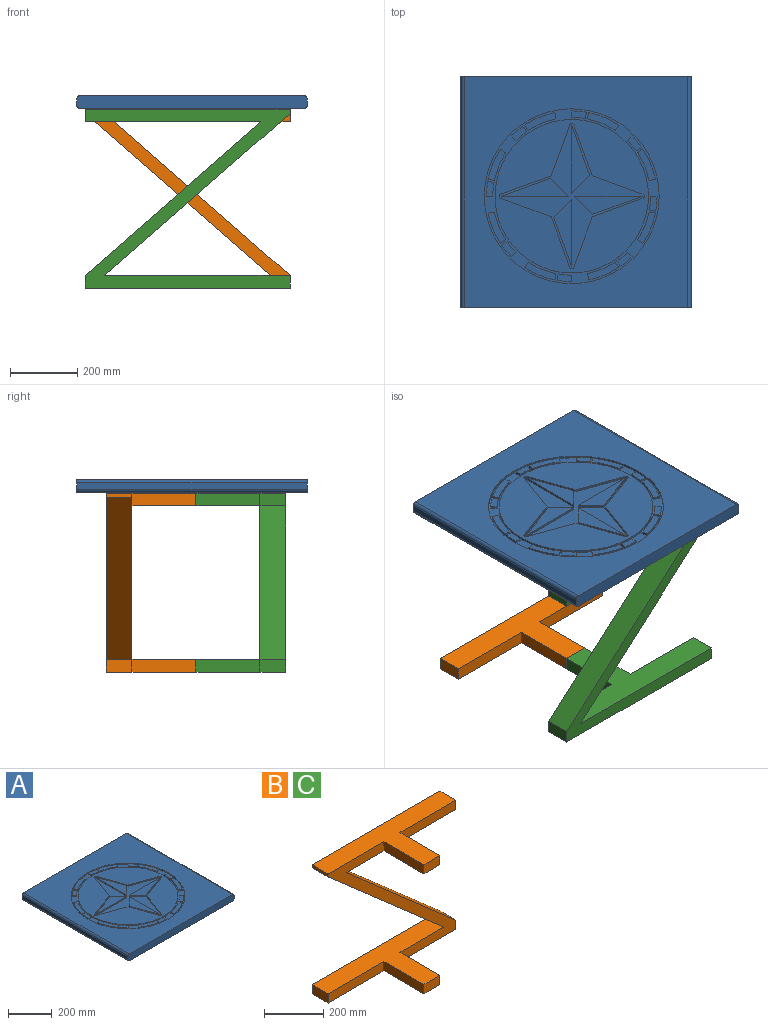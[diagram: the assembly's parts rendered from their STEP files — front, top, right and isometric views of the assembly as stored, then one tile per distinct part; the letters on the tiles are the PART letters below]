
ASSEMBLY  parts=3 mates=1
PART A: 123 faces, bbox 685.8x685.8x38.1 mm
  f0: plane 457.2x457.2mm, normal (0,0,1), area 108640mm2, adj f76,f96,f97,f98,f99,f100,f101,f102
  f1: plane 685.8x666.75mm, normal (0,0,1), area 244313.3mm2, adj f3,f5,f9,f10,f59
  f2: plane 685.8x19.05mm, normal (-1,0,0), area 13064.5mm2, adj f3,f5,f8,f10
  f3: plane 685.8x38.1mm, normal (0,-1,0), area 26051.1mm2, adj f1,f2,f4,f6,f7,f8,f9,f10
  f4: plane 685.8x19.05mm, normal (1,0,0), area 13064.5mm2, adj f3,f5,f7,f9
  f5: plane 685.8x38.1mm, normal (0,1,0), area 26051.1mm2, adj f1,f2,f4,f6,f7,f8,f9,f10
  f6: plane 685.8x666.75mm, normal (0,0,-1), area 457257.1mm2, adj f3,f5,f7,f8
  f7: cylinder r=9.53mm len=685.8mm, axis (0,1,0), area 10260.8mm2, adj f3,f4,f5,f6
  f8: cylinder r=9.53mm len=685.8mm, axis (0,-1,0), area 10260.8mm2, adj f2,f3,f5,f6
  f9: cylinder r=9.53mm len=685.8mm, axis (0,-1,0), area 10260.8mm2, adj f1,f3,f4,f5
  f10: cylinder r=9.53mm len=685.8mm, axis (0,1,0), area 10260.8mm2, adj f1,f2,f3,f5
  f11: cylinder r=254mm len=90.1mm, axis (0,0,1), area 623.1mm2, adj f12,f60,f77,f93
  f12: plane 18.77x6.35mm, normal (0.17,-0.98,0), area 121mm2, adj f11,f13,f77,f93
  f13: cylinder r=234.95mm len=82.47mm, axis (0,0,1), area 570.3mm2, adj f12,f60,f77,f93
  f14: cylinder r=254mm len=33.92mm, axis (0,0,1), area 281.5mm2, adj f15,f61,f77,f92
  f15: plane 15.61x10.93mm, normal (0.57,-0.82,0), area 121mm2, adj f14,f16,f77,f92
  f16: cylinder r=234.95mm len=31.37mm, axis (0,0,1), area 260.4mm2, adj f15,f61,f77,f92
  f17: cylinder r=254mm len=33.92mm, axis (0,0,1), area 281.5mm2, adj f18,f62,f77,f91
  f18: plane 15.61x10.93mm, normal (0.82,0.57,0), area 121mm2, adj f17,f19,f77,f91
  f19: cylinder r=234.95mm len=31.37mm, axis (0,0,1), area 260.4mm2, adj f18,f62,f77,f91
  f20: cylinder r=254mm len=90.1mm, axis (0,0,1), area 623.1mm2, adj f21,f63,f77,f90
  f21: plane 15.61x10.93mm, normal (0.57,0.82,0), area 121mm2, adj f20,f22,f77,f90
  f22: cylinder r=234.95mm len=82.47mm, axis (0,0,1), area 570.3mm2, adj f21,f63,f77,f90
  f23: cylinder r=254mm len=44.11mm, axis (0,0,1), area 281.5mm2, adj f24,f64,f77,f89
  f24: plane 18.76x6.35mm, normal (0.17,0.98,0), area 121mm2, adj f23,f25,f77,f89
  f25: cylinder r=234.95mm len=40.8mm, axis (0,0,1), area 260.4mm2, adj f24,f64,f77,f89
  f26: cylinder r=254mm len=90.1mm, axis (0,0,1), area 623.1mm2, adj f27,f65,f77,f88
  f27: plane 18.77x6.35mm, normal (-0.17,0.98,0), area 121mm2, adj f26,f28,f77,f88
  f28: cylinder r=234.95mm len=82.47mm, axis (0,0,1), area 570.3mm2, adj f27,f65,f77,f88
  f29: cylinder r=254mm len=33.92mm, axis (0,0,1), area 281.5mm2, adj f30,f66,f77,f87
  f30: plane 15.61x10.93mm, normal (-0.57,0.82,0), area 121mm2, adj f29,f31,f77,f87
  f31: cylinder r=234.95mm len=31.37mm, axis (0,0,1), area 260.4mm2, adj f30,f66,f77,f87
  f32: cylinder r=254mm len=90.1mm, axis (0,0,1), area 623.1mm2, adj f33,f67,f77,f86
  f33: plane 15.61x10.93mm, normal (-0.82,0.57,0), area 121mm2, adj f32,f34,f77,f86
  f34: cylinder r=234.95mm len=82.47mm, axis (0,0,1), area 570.3mm2, adj f33,f67,f77,f86
  f35: cylinder r=254mm len=44.11mm, axis (0,0,1), area 281.5mm2, adj f36,f68,f77,f85
  f36: plane 18.76x6.35mm, normal (-0.98,0.17,0), area 121mm2, adj f35,f37,f77,f85
  f37: cylinder r=234.95mm len=40.8mm, axis (0,0,1), area 260.4mm2, adj f36,f68,f77,f85
  f38: cylinder r=254mm len=90.1mm, axis (0,0,1), area 623.1mm2, adj f39,f69,f77,f84
  f39: plane 18.77x6.35mm, normal (-0.98,-0.17,0), area 121mm2, adj f38,f40,f77,f84
  f40: cylinder r=234.95mm len=82.47mm, axis (0,0,1), area 570.3mm2, adj f39,f69,f77,f84
  f41: cylinder r=254mm len=33.92mm, axis (0,0,1), area 281.5mm2, adj f42,f70,f77,f83
  f42: plane 15.61x10.93mm, normal (-0.82,-0.57,0), area 121mm2, adj f41,f43,f77,f83
  f43: cylinder r=234.95mm len=31.37mm, axis (0,0,1), area 260.4mm2, adj f42,f70,f77,f83
  f44: cylinder r=254mm len=90.1mm, axis (0,0,1), area 623.1mm2, adj f45,f71,f77,f82
  f45: plane 15.61x10.93mm, normal (-0.57,-0.82,0), area 121mm2, adj f44,f46,f77,f82
  f46: cylinder r=234.95mm len=82.47mm, axis (0,0,1), area 570.3mm2, adj f45,f71,f77,f82
  f47: cylinder r=254mm len=44.11mm, axis (0,0,1), area 281.5mm2, adj f48,f72,f77,f81
  f48: plane 18.76x6.35mm, normal (-0.17,-0.98,0), area 121mm2, adj f47,f49,f77,f81
  f49: cylinder r=234.95mm len=40.8mm, axis (0,0,1), area 260.4mm2, adj f48,f72,f77,f81
  f50: cylinder r=234.95mm len=82.47mm, axis (0,0,1), area 570.3mm2, adj f51,f73,f77,f80
  f51: plane 18.77x6.35mm, normal (-0.98,0.17,0), area 121mm2, adj f50,f52,f77,f80
  f52: cylinder r=254mm len=90.1mm, axis (0,0,1), area 623.1mm2, adj f51,f73,f77,f80
  f53: plane 18.77x6.35mm, normal (0.98,0.17,0), area 121mm2, adj f54,f74,f77,f79
  f54: cylinder r=234.95mm len=82.47mm, axis (0,0,1), area 570.3mm2, adj f53,f55,f77,f79
  f55: plane 15.61x10.93mm, normal (-0.82,-0.57,0), area 121mm2, adj f54,f74,f77,f79
  f56: cylinder r=234.95mm len=40.8mm, axis (0,0,1), area 260.4mm2, adj f57,f75,f77,f78
  f57: plane 19.05x6.35mm, normal (-1,0,0), area 121mm2, adj f56,f58,f77,f78
  f58: cylinder r=254mm len=44.11mm, axis (0,0,1), area 281.5mm2, adj f57,f75,f77,f78
  f59: cylinder r=260.35mm len=520.7mm, axis (0,0,1), area 10387.5mm2, adj f1,f77
  f60: plane 15.61x10.93mm, normal (-0.57,0.82,0), area 121mm2, adj f11,f13,f77,f93
  f61: plane 13.47x13.47mm, normal (-0.71,0.71,0), area 121mm2, adj f14,f16,f77,f92
  f62: plane 13.47x13.47mm, normal (-0.71,-0.71,0), area 121mm2, adj f17,f19,f77,f91
  f63: plane 18.77x6.35mm, normal (-0.17,-0.98,0), area 121mm2, adj f20,f22,f77,f90
  f64: plane 19.05x6.35mm, normal (0,-1,0), area 121mm2, adj f23,f25,f77,f89
  f65: plane 15.61x10.93mm, normal (0.57,-0.82,0), area 121mm2, adj f26,f28,f77,f88
  f66: plane 13.47x13.47mm, normal (0.71,-0.71,0), area 121mm2, adj f29,f31,f77,f87
  f67: plane 18.77x6.35mm, normal (0.98,-0.17,0), area 121mm2, adj f32,f34,f77,f86
  f68: plane 19.05x6.35mm, normal (1,0,0), area 121mm2, adj f35,f37,f77,f85
  f69: plane 15.61x10.93mm, normal (0.82,0.57,0), area 121mm2, adj f38,f40,f77,f84
  f70: plane 13.47x13.47mm, normal (0.71,0.71,0), area 121mm2, adj f41,f43,f77,f83
  f71: plane 18.77x6.35mm, normal (0.17,0.98,0), area 121mm2, adj f44,f46,f77,f82
  f72: plane 19.05x6.35mm, normal (0,1,0), area 121mm2, adj f47,f49,f77,f81
  f73: plane 15.61x10.93mm, normal (0.82,-0.57,0), area 121mm2, adj f50,f52,f77,f80
  f74: cylinder r=254mm len=90.1mm, axis (0,0,1), area 623.1mm2, adj f53,f55,f77,f79
  f75: plane 18.76x6.35mm, normal (0.98,-0.17,0), area 121mm2, adj f56,f58,f77,f78
  f76: cylinder r=228.6mm len=457.2mm, axis (0,0,1), area 9120.7mm2, adj f0,f77
  f77: plane 520.7x520.7mm, normal (0,0,1), area 27946.7mm2, adj f11,f12,f13,f14,f15,f16,f17,f18
  f78: plane 44.11x22.62mm, normal (0,0,1), area 812.8mm2, adj f56,f57,f58,f75
  f79: plane 93.4x52.93mm, normal (0,0,1), area 1790.1mm2, adj f53,f54,f55,f74
  f80: plane 93.4x52.93mm, normal (0,0,1), area 1790.1mm2, adj f50,f51,f52,f73
  f81: plane 44.11x22.62mm, normal (0,0,1), area 812.8mm2, adj f47,f48,f49,f72
  f82: plane 93.4x52.93mm, normal (0,0,1), area 1790.1mm2, adj f44,f45,f46,f71
  f83: plane 44.84x41.93mm, normal (0,0,1), area 812.8mm2, adj f41,f42,f43,f70
  f84: plane 93.4x52.93mm, normal (0,0,1), area 1790.1mm2, adj f38,f39,f40,f69
  f85: plane 44.11x22.62mm, normal (0,0,1), area 812.8mm2, adj f35,f36,f37,f68
  f86: plane 93.4x52.93mm, normal (0,0,1), area 1790.1mm2, adj f32,f33,f34,f67
  f87: plane 44.84x41.93mm, normal (0,0,1), area 812.8mm2, adj f29,f30,f31,f66
  f88: plane 93.4x52.93mm, normal (0,0,1), area 1790.1mm2, adj f26,f27,f28,f65
  f89: plane 44.11x22.62mm, normal (0,0,1), area 812.8mm2, adj f23,f24,f25,f64
  f90: plane 93.4x52.93mm, normal (0,0,1), area 1790.1mm2, adj f20,f21,f22,f63
  f91: plane 44.84x41.93mm, normal (0,0,1), area 812.8mm2, adj f17,f18,f19,f62
  f92: plane 44.84x41.93mm, normal (0,0,1), area 812.8mm2, adj f14,f15,f16,f61
  f93: plane 93.4x52.93mm, normal (0,0,1), area 1790.1mm2, adj f11,f12,f13,f60
  f94: plane 147.4x53.65mm, normal (-0.34,0.94,0), area 996.1mm2, adj f95,f114,f115,f116
  f95: plane 53.65x53.65mm, normal (0.71,0.71,0), area 481.8mm2, adj f94,f114,f115,f116
  f96: plane 151.2x55.03mm, normal (-0.34,0.94,0), area 1021.8mm2, adj f0,f97,f112,f116
  f97: cylinder r=6.35mm len=11.93mm, axis (0,0,1), area 98.5mm2, adj f0,f96,f98,f116
  f98: plane 151.2x55.03mm, normal (-0.34,-0.94,0), area 1021.8mm2, adj f0,f97,f99,f116
  f99: plane 151.2x55.03mm, normal (-0.94,-0.34,0), area 1021.8mm2, adj f0,f98,f100,f116
  f100: cylinder r=6.35mm len=11.93mm, axis (0,0,1), area 98.5mm2, adj f0,f99,f101,f116
  f101: plane 151.2x55.03mm, normal (0.94,-0.34,0), area 1021.8mm2, adj f0,f100,f102,f116
  f102: plane 151.2x55.03mm, normal (0.34,-0.94,0), area 1021.8mm2, adj f0,f101,f103,f116
  f103: cylinder r=6.35mm len=11.93mm, axis (0,0,1), area 98.5mm2, adj f0,f102,f104,f116
  f104: plane 151.2x55.03mm, normal (0.34,0.94,0), area 1021.8mm2, adj f0,f103,f105,f116
  f105: plane 151.2x55.03mm, normal (0.94,0.34,0), area 1021.8mm2, adj f0,f104,f106,f116
  f106: cylinder r=6.35mm len=11.93mm, axis (0,0,1), area 98.5mm2, adj f0,f105,f112,f116
  f107: plane 147.4x53.65mm, normal (-0.94,-0.34,0), area 996.1mm2, adj f108,f116,f117,f118
  f108: plane 53.65x53.65mm, normal (-0.71,0.71,0), area 481.8mm2, adj f107,f116,f117,f118
  f109: plane 147.4x53.65mm, normal (0.34,-0.94,0), area 996.1mm2, adj f113,f116,f119,f120
  f110: plane 147.4x53.65mm, normal (0.94,0.34,0), area 996.1mm2, adj f111,f116,f121,f122
  f111: plane 53.65x53.65mm, normal (0.71,-0.71,0), area 481.8mm2, adj f110,f116,f121,f122
  f112: plane 151.2x55.03mm, normal (-0.94,0.34,0), area 1021.8mm2, adj f0,f96,f106,f116
  f113: plane 53.65x53.65mm, normal (-0.71,-0.71,0), area 481.8mm2, adj f109,f116,f119,f120
  f114: plane 201.05x53.65mm, normal (0,0,1), area 5393.3mm2, adj f94,f95,f115
  f115: plane 201.05x6.35mm, normal (0,-1,0), area 1276.7mm2, adj f94,f95,f114,f116
  f116: plane 432.77x432.77mm, normal (0,0,1), area 33960.1mm2, adj f94,f95,f96,f97,f98,f99,f100,f101
  f117: plane 201.05x53.65mm, normal (0,0,1), area 5393.3mm2, adj f107,f108,f118
  f118: plane 201.05x6.35mm, normal (1,0,0), area 1276.7mm2, adj f107,f108,f116,f117
  f119: plane 201.05x53.65mm, normal (0,0,1), area 5393.3mm2, adj f109,f113,f120
  f120: plane 201.05x6.35mm, normal (0,1,0), area 1276.7mm2, adj f109,f113,f116,f119
  f121: plane 201.05x53.65mm, normal (0,0,1), area 5393.3mm2, adj f110,f111,f122
  f122: plane 201.05x6.35mm, normal (-1,0,0), area 1276.7mm2, adj f110,f111,f116,f121
PART B: 20 faces, bbox 609.6x266.7x533.4 mm
  f0: plane 266.7x38.1mm, normal (0,-1,0), area 10161.3mm2, adj f6,f7,f8,f18
  f1: plane 266.7x38.1mm, normal (0,-1,0), area 10161.3mm2, adj f2,f3,f11,f14
  f2: plane 76.2x38.1mm, normal (-1,0,0), area 2903.2mm2, adj f1,f3,f11,f13
  f3: plane 609.6x266.7mm, normal (0,0,-1), area 60967.6mm2, adj f1,f2,f4,f12,f13,f14,f15,f16
  f4: plane 76.2x38.1mm, normal (1,0,0), area 2903.2mm2, adj f3,f5,f12,f13
  f5: plane 522.69x457.2mm, normal (0.66,0,0.75), area 52915.9mm2, adj f4,f6,f12,f13
  f6: plane 522.69x266.7mm, normal (0,0,-1), area 54345.2mm2, adj f0,f5,f7,f12,f13,f17,f18,f19
  f7: plane 76.2x38.1mm, normal (1,0,0), area 2903.2mm2, adj f0,f6,f8,f13
  f8: plane 609.6x266.7mm, normal (0,0,1), area 60967.6mm2, adj f0,f7,f9,f12,f13,f17,f18,f19
  f9: plane 76.2x12.7mm, normal (-1,0,0), area 967.7mm2, adj f8,f10,f12,f13
  f10: plane 551.73x482.6mm, normal (-0.66,0,-0.75), area 55855.7mm2, adj f9,f11,f12,f13
  f11: plane 551.73x266.7mm, normal (0,0,1), area 56558mm2, adj f1,f2,f10,f12,f13,f14,f15,f16
  f12: plane 609.6x533.4mm, normal (0,-1,0), area 46411.7mm2, adj f3,f4,f5,f6,f8,f9,f10,f11
  f13: plane 609.6x533.4mm, normal (0,1,0), area 72540.7mm2, adj f2,f3,f4,f5,f6,f7,f8,f9
  f14: plane 190.5x38.1mm, normal (-1,0,0), area 7258mm2, adj f1,f3,f11,f16
  f15: plane 190.5x38.1mm, normal (1,0,0), area 7258mm2, adj f3,f11,f12,f16
  f16: plane 76.2x38.1mm, normal (0,-1,0), area 2903.2mm2, adj f3,f11,f14,f15
  f17: plane 190.5x38.1mm, normal (-1,0,0), area 7258mm2, adj f6,f8,f12,f19
  f18: plane 190.5x38.1mm, normal (1,0,0), area 7258mm2, adj f0,f6,f8,f19
  f19: plane 76.2x38.1mm, normal (0,-1,0), area 2903.2mm2, adj f6,f8,f17,f18
PART C: same geometry as B
PLACE A t=(75.29,380.36,432.39)mm
PLACE B t=(-229.67,647.92,-102.84)mm
PLACE C rot(axis=(0,0,1),180deg) t=(379.93,114.52,-102.84)mm
MATE fastened B.f8 <-> C.f8  axis (0,0,1) through (246.58,571.72,430.56)mm
